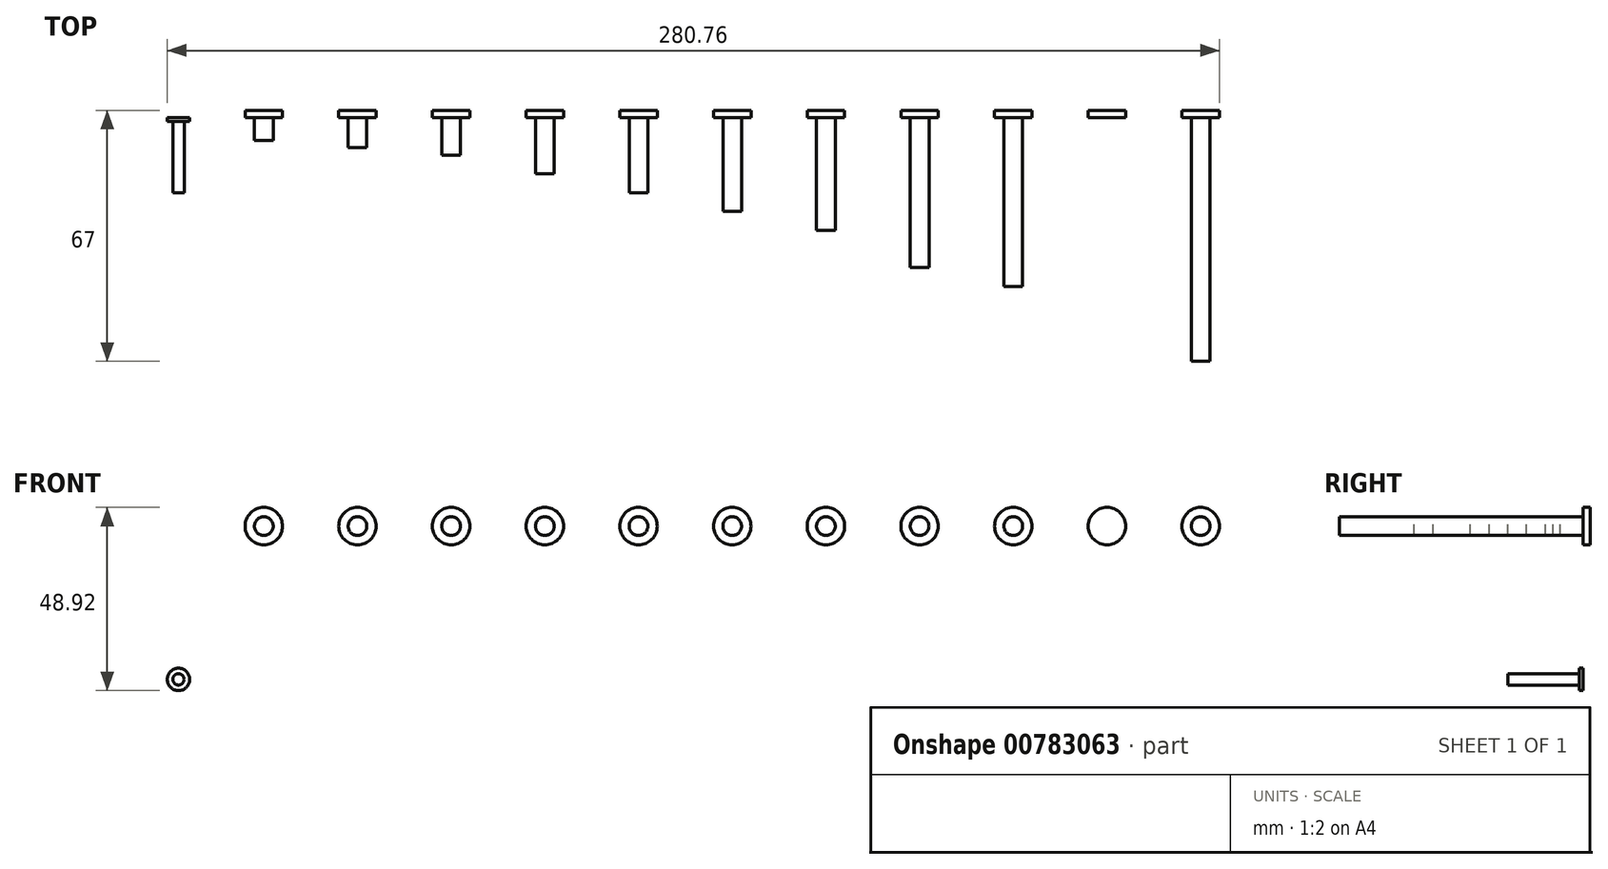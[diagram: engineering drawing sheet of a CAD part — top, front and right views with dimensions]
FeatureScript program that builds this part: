
annotation { "Feature Type Name" : "Feature", "Feature Type Description" : "" }
export const myFeature = defineFeature(function(context is Context, id is Id, definition is map)
    precondition{}
    {
        {
            var Q0;
            Q0=qCreatedBy(makeId("Front.planeOp"),FACE);
            var sketch = newSketch(context, id + "F0", { "sketchPlane" : qUnion([Q0])});
            skCircle(sketch, "E0", {"center": v(-18.92, -7.26) * mm, "radius": 5 * mm});
            skCircle(sketch, "E1", {"center": v(-18.92, -7.26) * mm, "radius": 2.5 * mm});
            skCircle(sketch, "E2.1.0.0", {"center": v(6.08, -7.26) * mm, "radius": 2.5 * mm});
            skCircle(sketch, "E2.1.0.1", {"center": v(6.08, -7.26) * mm, "radius": 5 * mm});
            skCircle(sketch, "E2.2.0.0", {"center": v(31.08, -7.26) * mm, "radius": 2.5 * mm});
            skCircle(sketch, "E2.2.0.1", {"center": v(31.08, -7.26) * mm, "radius": 5 * mm});
            skCircle(sketch, "E2.3.0.0", {"center": v(56.08, -7.26) * mm, "radius": 2.5 * mm});
            skCircle(sketch, "E2.3.0.1", {"center": v(56.08, -7.26) * mm, "radius": 5 * mm});
            skCircle(sketch, "E2.4.0.0", {"center": v(81.08, -7.26) * mm, "radius": 2.5 * mm});
            skCircle(sketch, "E2.4.0.1", {"center": v(81.08, -7.26) * mm, "radius": 5 * mm});
            skLineSegment(sketch, "E2.direction1", {"start": v(-18.92, -7.26) * mm, "end": v(6.08, -7.26) * mm, "construction": true});
            skCircle(sketch, "E3.0.5.0", {"center": v(106.08, -7.26) * mm, "radius": 2.5 * mm});
            skCircle(sketch, "E3.2.5.0", {"center": v(106.08, -7.26) * mm, "radius": 5 * mm});
            skCircle(sketch, "E3.0.6.0", {"center": v(131.08, -7.26) * mm, "radius": 2.5 * mm});
            skCircle(sketch, "E3.2.6.0", {"center": v(131.08, -7.26) * mm, "radius": 5 * mm});
            skCircle(sketch, "E3.0.7.0", {"center": v(156.08, -7.26) * mm, "radius": 2.5 * mm});
            skCircle(sketch, "E3.2.7.0", {"center": v(156.08, -7.26) * mm, "radius": 5 * mm});
            skCircle(sketch, "E3.0.8.0", {"center": v(181.08, -7.26) * mm, "radius": 2.5 * mm});
            skCircle(sketch, "E3.2.8.0", {"center": v(181.08, -7.26) * mm, "radius": 5 * mm});
            skCircle(sketch, "E3.0.9.0", {"center": v(206.08, -7.26) * mm, "radius": 2.5 * mm});
            skCircle(sketch, "E3.2.9.0", {"center": v(206.08, -7.26) * mm, "radius": 5 * mm});
            skCircle(sketch, "E4.0.10.0", {"center": v(231.08, -7.26) * mm, "radius": 2.5 * mm});
            skCircle(sketch, "E4.2.10.0", {"center": v(231.08, -7.26) * mm, "radius": 5 * mm});
            skCircle(sketch, "E5", {"center": v(-41.68, -48.18) * mm, "radius": 3 * mm});
            skCircle(sketch, "E6", {"center": v(-41.68, -48.18) * mm, "radius": 1.5 * mm});
            skSolve(sketch);
        }
        {
            var Q0;
            Q0=makeQuery(id+"F0.imprint","IMPRINT",FACE,{"disambiguationData":[TD([[makeQuery(id+"F0.imprint","IMPRINT",EDGE,{"derivedFrom":sQuery(id+"F0.wireOp",EDGE,"E1")}),1.0]])]});
            var Q1;
            Q1=makeQuery(id+"F0.imprint","IMPRINT",FACE,{"disambiguationData":[TD([[makeQuery(id+"F0.imprint","IMPRINT",EDGE,{"derivedFrom":sQuery(id+"F0.wireOp",EDGE,"E0")}),1.0]])]});
            var Q2;
            Q2=makeQuery(id+"F0.imprint","IMPRINT",FACE,{"disambiguationData":[TD([[makeQuery(id+"F0.imprint","IMPRINT",EDGE,{"derivedFrom":sQuery(id+"F0.wireOp",EDGE,"E2.1.0.0")}),-1.0]])]});
            var Q3;
            Q3=makeQuery(id+"F0.imprint","IMPRINT",FACE,{"disambiguationData":[TD([[makeQuery(id+"F0.imprint","IMPRINT",EDGE,{"derivedFrom":sQuery(id+"F0.wireOp",EDGE,"E2.1.0.0")}),1.0]])]});
            var Q4;
            Q4=makeQuery(id+"F0.imprint","IMPRINT",FACE,{"disambiguationData":[TD([[makeQuery(id+"F0.imprint","IMPRINT",EDGE,{"derivedFrom":sQuery(id+"F0.wireOp",EDGE,"E2.2.0.0")}),1.0]])]});
            var Q5;
            Q5=makeQuery(id+"F0.imprint","IMPRINT",FACE,{"disambiguationData":[TD([[makeQuery(id+"F0.imprint","IMPRINT",EDGE,{"derivedFrom":sQuery(id+"F0.wireOp",EDGE,"E2.2.0.0")}),-1.0]])]});
            var Q6;
            Q6=makeQuery(id+"F0.imprint","IMPRINT",FACE,{"disambiguationData":[TD([[makeQuery(id+"F0.imprint","IMPRINT",EDGE,{"derivedFrom":sQuery(id+"F0.wireOp",EDGE,"E2.3.0.0")}),1.0]])]});
            var Q7;
            Q7=makeQuery(id+"F0.imprint","IMPRINT",FACE,{"disambiguationData":[TD([[makeQuery(id+"F0.imprint","IMPRINT",EDGE,{"derivedFrom":sQuery(id+"F0.wireOp",EDGE,"E2.3.0.0")}),-1.0]])]});
            var Q8;
            Q8=makeQuery(id+"F0.imprint","IMPRINT",FACE,{"disambiguationData":[TD([[makeQuery(id+"F0.imprint","IMPRINT",EDGE,{"derivedFrom":sQuery(id+"F0.wireOp",EDGE,"E3.0.7.0")}),1.0]])]});
            var Q9;
            Q9=makeQuery(id+"F0.imprint","IMPRINT",FACE,{"disambiguationData":[TD([[makeQuery(id+"F0.imprint","IMPRINT",EDGE,{"derivedFrom":sQuery(id+"F0.wireOp",EDGE,"E3.0.6.0")}),-1.0]])]});
            var Q10;
            Q10=makeQuery(id+"F0.imprint","IMPRINT",FACE,{"disambiguationData":[TD([[makeQuery(id+"F0.imprint","IMPRINT",EDGE,{"derivedFrom":sQuery(id+"F0.wireOp",EDGE,"E3.0.7.0")}),-1.0]])]});
            var Q11;
            Q11=makeQuery(id+"F0.imprint","IMPRINT",FACE,{"disambiguationData":[TD([[makeQuery(id+"F0.imprint","IMPRINT",EDGE,{"derivedFrom":sQuery(id+"F0.wireOp",EDGE,"E3.0.6.0")}),1.0]])]});
            var Q12;
            Q12=makeQuery(id+"F0.imprint","IMPRINT",FACE,{"disambiguationData":[TD([[makeQuery(id+"F0.imprint","IMPRINT",EDGE,{"derivedFrom":sQuery(id+"F0.wireOp",EDGE,"E3.0.5.0")}),-1.0]])]});
            var Q13;
            Q13=makeQuery(id+"F0.imprint","IMPRINT",FACE,{"disambiguationData":[TD([[makeQuery(id+"F0.imprint","IMPRINT",EDGE,{"derivedFrom":sQuery(id+"F0.wireOp",EDGE,"E3.0.5.0")}),1.0]])]});
            var Q14;
            Q14=makeQuery(id+"F0.imprint","IMPRINT",FACE,{"disambiguationData":[TD([[makeQuery(id+"F0.imprint","IMPRINT",EDGE,{"derivedFrom":sQuery(id+"F0.wireOp",EDGE,"E2.4.0.0")}),1.0]])]});
            var Q15;
            Q15=makeQuery(id+"F0.imprint","IMPRINT",FACE,{"disambiguationData":[TD([[makeQuery(id+"F0.imprint","IMPRINT",EDGE,{"derivedFrom":sQuery(id+"F0.wireOp",EDGE,"E2.4.0.0")}),-1.0]])]});
            var Q16;
            Q16=makeQuery(id+"F0.imprint","IMPRINT",FACE,{"disambiguationData":[TD([[makeQuery(id+"F0.imprint","IMPRINT",EDGE,{"derivedFrom":sQuery(id+"F0.wireOp",EDGE,"E3.0.9.0")}),1.0]])]});
            var Q17;
            Q17=makeQuery(id+"F0.imprint","IMPRINT",FACE,{"disambiguationData":[TD([[makeQuery(id+"F0.imprint","IMPRINT",EDGE,{"derivedFrom":sQuery(id+"F0.wireOp",EDGE,"E3.0.9.0")}),-1.0]])]});
            var Q18;
            Q18=makeQuery(id+"F0.imprint","IMPRINT",FACE,{"disambiguationData":[TD([[makeQuery(id+"F0.imprint","IMPRINT",EDGE,{"derivedFrom":sQuery(id+"F0.wireOp",EDGE,"E3.0.8.0")}),1.0]])]});
            var Q19;
            Q19=makeQuery(id+"F0.imprint","IMPRINT",FACE,{"disambiguationData":[TD([[makeQuery(id+"F0.imprint","IMPRINT",EDGE,{"derivedFrom":sQuery(id+"F0.wireOp",EDGE,"E3.0.8.0")}),-1.0]])]});
            var Q20;
            Q20=makeQuery(id+"F0.imprint","IMPRINT",FACE,{"disambiguationData":[TD([[makeQuery(id+"F0.imprint","IMPRINT",EDGE,{"derivedFrom":sQuery(id+"F0.wireOp",EDGE,"E4.0.10.0")}),-1.0]])]});
            var Q21;
            Q21=makeQuery(id+"F0.imprint","IMPRINT",FACE,{"disambiguationData":[TD([[makeQuery(id+"F0.imprint","IMPRINT",EDGE,{"derivedFrom":sQuery(id+"F0.wireOp",EDGE,"E4.0.10.0")}),1.0]])]});
            extrude(context, id + "F1", {"entities" : qUnion([Q0, Q1, Q2, Q3, Q4, Q5, Q6, Q7, Q8, Q9, Q10, Q11, Q12, Q13, Q14, Q15, Q16, Q17, Q18, Q19, Q20, Q21]), "oppositeDirection" : true, "depth" : 2 * mm, "offsetDistance" : 25 * mm});
        }
        {
            var Q0;
            Q0=makeQuery(id+"F0.imprint","IMPRINT",FACE,{"disambiguationData":[TD([[makeQuery(id+"F0.imprint","IMPRINT",EDGE,{"derivedFrom":sQuery(id+"F0.wireOp",EDGE,"E1")}),1.0]])]});
            extrude(context, id + "F2", {"entities" : qUnion([Q0]), "operationType" : NewBodyOperationType.ADD, "depth" : 6 * mm, "offsetDistance" : 25 * mm});
        }
        {
            var Q0;
            Q0=makeQuery(id+"F0.imprint","IMPRINT",FACE,{"disambiguationData":[TD([[makeQuery(id+"F0.imprint","IMPRINT",EDGE,{"derivedFrom":sQuery(id+"F0.wireOp",EDGE,"E2.1.0.0")}),1.0]])]});
            extrude(context, id + "F3", {"entities" : qUnion([Q0]), "operationType" : NewBodyOperationType.ADD, "depth" : 8 * mm, "offsetDistance" : 25 * mm});
        }
        {
            var Q0;
            Q0=makeQuery(id+"F0.imprint","IMPRINT",FACE,{"disambiguationData":[TD([[makeQuery(id+"F0.imprint","IMPRINT",EDGE,{"derivedFrom":sQuery(id+"F0.wireOp",EDGE,"E2.2.0.0")}),1.0]])]});
            extrude(context, id + "F4", {"entities" : qUnion([Q0]), "operationType" : NewBodyOperationType.ADD, "depth" : 10 * mm, "offsetDistance" : 25 * mm});
        }
        {
            var Q0;
            Q0=makeQuery(id+"F0.imprint","IMPRINT",FACE,{"disambiguationData":[TD([[makeQuery(id+"F0.imprint","IMPRINT",EDGE,{"derivedFrom":sQuery(id+"F0.wireOp",EDGE,"E2.3.0.0")}),1.0]])]});
            extrude(context, id + "F5", {"entities" : qUnion([Q0]), "operationType" : NewBodyOperationType.ADD, "depth" : 15 * mm, "offsetDistance" : 25 * mm});
        }
        {
            var Q0;
            Q0=makeQuery(id+"F0.imprint","IMPRINT",FACE,{"disambiguationData":[TD([[makeQuery(id+"F0.imprint","IMPRINT",EDGE,{"derivedFrom":sQuery(id+"F0.wireOp",EDGE,"E2.4.0.0")}),1.0]])]});
            extrude(context, id + "F6", {"entities" : qUnion([Q0]), "operationType" : NewBodyOperationType.ADD, "depth" : 20 * mm, "offsetDistance" : 25 * mm});
        }
        {
            var Q0;
            Q0=makeQuery(id+"F0.imprint","IMPRINT",FACE,{"disambiguationData":[TD([[makeQuery(id+"F0.imprint","IMPRINT",EDGE,{"derivedFrom":sQuery(id+"F0.wireOp",EDGE,"E3.0.5.0")}),1.0]])]});
            extrude(context, id + "F7", {"entities" : qUnion([Q0]), "operationType" : NewBodyOperationType.ADD, "depth" : 25 * mm, "offsetDistance" : 25 * mm});
        }
        {
            var Q0;
            Q0=makeQuery(id+"F0.imprint","IMPRINT",FACE,{"disambiguationData":[TD([[makeQuery(id+"F0.imprint","IMPRINT",EDGE,{"derivedFrom":sQuery(id+"F0.wireOp",EDGE,"E3.0.6.0")}),1.0]])]});
            var Q1;
            Q1=sQuery(id+"F0.wireOp",EDGE,"E3.0.6.0");
            extrude(context, id + "F8", {"entities" : qUnion([Q0]), "operationType" : NewBodyOperationType.ADD, "surfaceEntities" : qUnion([Q1]), "depth" : 30 * mm, "offsetDistance" : 25 * mm});
        }
        {
            var Q0;
            Q0=makeQuery(id+"F0.imprint","IMPRINT",FACE,{"disambiguationData":[TD([[makeQuery(id+"F0.imprint","IMPRINT",EDGE,{"derivedFrom":sQuery(id+"F0.wireOp",EDGE,"E3.0.7.0")}),1.0]])]});
            extrude(context, id + "F9", {"entities" : qUnion([Q0]), "operationType" : NewBodyOperationType.ADD, "depth" : 40 * mm, "offsetDistance" : 25 * mm});
        }
        {
            var Q0;
            Q0=makeQuery(id+"F0.imprint","IMPRINT",FACE,{"disambiguationData":[TD([[makeQuery(id+"F0.imprint","IMPRINT",EDGE,{"derivedFrom":sQuery(id+"F0.wireOp",EDGE,"E3.0.8.0")}),1.0]])]});
            extrude(context, id + "F10", {"entities" : qUnion([Q0]), "operationType" : NewBodyOperationType.ADD, "depth" : 45 * mm, "offsetDistance" : 25 * mm});
        }
        {
            var Q0;
            Q0=sQuery(id+"F0.wireOp",EDGE,"E3.0.9.0");
            extrude(context, id + "F11", {"bodyType" : ToolBodyType.SURFACE, "surfaceEntities" : qUnion([Q0]), "depth" : 55 * mm, "offsetDistance" : 25 * mm});
        }
        {
            var Q0;
            Q0=makeQuery(id+"F0.imprint","IMPRINT",FACE,{"disambiguationData":[TD([[makeQuery(id+"F0.imprint","IMPRINT",EDGE,{"derivedFrom":sQuery(id+"F0.wireOp",EDGE,"E4.0.10.0")}),1.0]])]});
            extrude(context, id + "F12", {"entities" : qUnion([Q0]), "operationType" : NewBodyOperationType.ADD, "depth" : 65 * mm, "offsetDistance" : 25 * mm});
        }
        {
            var Q0;
            Q0=makeQuery(id+"F0.imprint","IMPRINT",FACE,{"disambiguationData":[TD([[makeQuery(id+"F0.imprint","IMPRINT",EDGE,{"derivedFrom":sQuery(id+"F0.wireOp",EDGE,"E5")}),1.0]])]});
            extrude(context, id + "F13", {"entities" : qUnion([Q0]), "depth" : 1 * mm, "offsetDistance" : 25 * mm});
        }
        {
            var Q0;
            Q0=makeQuery(id+"F0.imprint","IMPRINT",FACE,{"disambiguationData":[TD([[makeQuery(id+"F0.imprint","IMPRINT",EDGE,{"derivedFrom":sQuery(id+"F0.wireOp",EDGE,"E6")}),1.0]])]});
            extrude(context, id + "F14", {"entities" : qUnion([Q0]), "operationType" : NewBodyOperationType.ADD, "depth" : 20 * mm, "offsetDistance" : 25 * mm});
        }
    });
